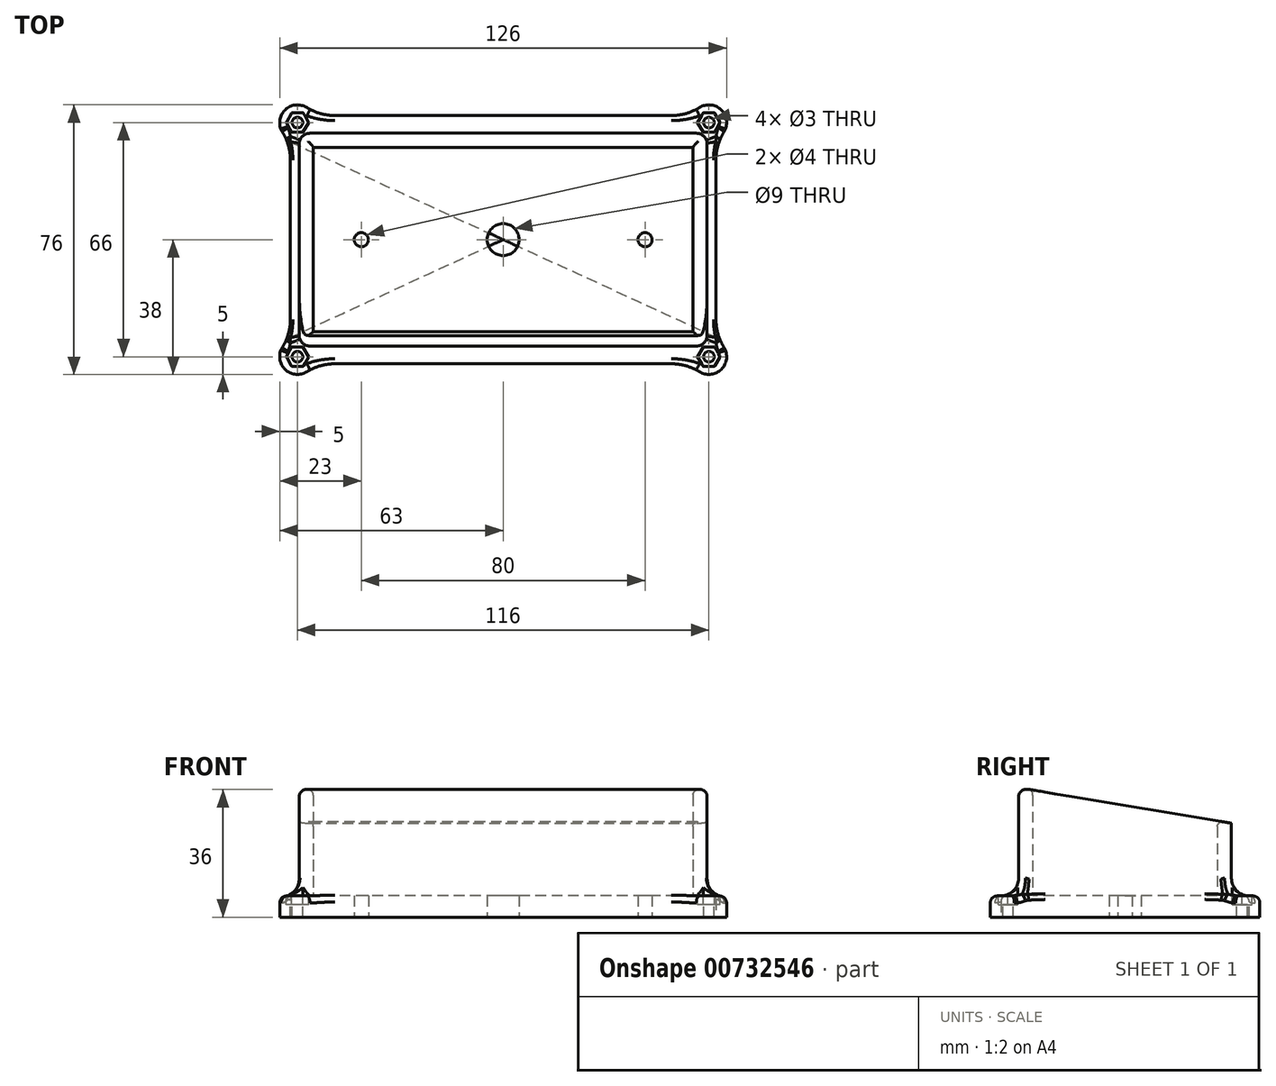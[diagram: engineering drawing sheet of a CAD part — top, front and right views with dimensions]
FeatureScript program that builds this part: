
annotation { "Feature Type Name" : "Feature", "Feature Type Description" : "" }
export const myFeature = defineFeature(function(context is Context, id is Id, definition is map)
    precondition{}
    {
        {
            var Q0;
            Q0=qCreatedBy(makeId("Top.planeOp"),FACE);
            var sketch = newSketch(context, id + "F0", { "sketchPlane" : qUnion([Q0])});
            skLineSegment(sketch, "E0.bottom", {"start": v(53.42, 35) * mm, "end": v(-53.42, 35) * mm});
            skLineSegment(sketch, "E0.top", {"start": v(53.42, -35) * mm, "end": v(-53.42, -35) * mm});
            skLineSegment(sketch, "E0.left", {"start": v(60, 28.42) * mm, "end": v(60, -28.42) * mm});
            skLineSegment(sketch, "E0.right", {"start": v(-60, 28.42) * mm, "end": v(-60, -28.42) * mm});
            skPoint(sketch, "E0.middle", {"position": v(0, 0) * mm});
            skLineSegment(sketch, "E1.bottom", {"start": v(58, -33) * mm, "end": v(-58, -33) * mm, "construction": true});
            skLineSegment(sketch, "E1.top", {"start": v(58, 33) * mm, "end": v(-58, 33) * mm, "construction": true});
            skLineSegment(sketch, "E1.left", {"start": v(58, 33) * mm, "end": v(58, -33) * mm, "construction": true});
            skLineSegment(sketch, "E1.right", {"start": v(-58, 33) * mm, "end": v(-58, -33) * mm, "construction": true});
            skArc(sketch, "E2", {"start": v(-53.42, 35) * mm, "mid": v(-61.54, 36.54) * mm, "end": v(-60, 28.42) * mm});
            skArc(sketch, "E3", {"start": v(-60, -28.42) * mm, "mid": v(-61.54, -36.54) * mm, "end": v(-53.42, -35) * mm});
            skArc(sketch, "E4", {"start": v(60, 28.42) * mm, "mid": v(61.54, 36.54) * mm, "end": v(53.42, 35) * mm});
            skArc(sketch, "E5", {"start": v(53.42, -35) * mm, "mid": v(61.54, -36.54) * mm, "end": v(60, -28.42) * mm});
            skPoint(sketch, "E6.orphan", {"position": v(-60, 35) * mm});
            skPoint(sketch, "E7.orphan", {"position": v(60, 35) * mm});
            skPoint(sketch, "E8.orphan", {"position": v(60, -35) * mm});
            skPoint(sketch, "E9.orphan", {"position": v(-60, -35) * mm});
            skSolve(sketch);
        }
        {
            var Q0;
            Q0 = qSketchRegion(id + "F0", true);
            extrude(context, id + "F1", {"entities" : qUnion([Q0]), "depth" : 6 * mm, "offsetDistance" : 25 * mm});
        }
        {
            var Q0;
            Q0=makeQuery(id+"F1.opExtrude","SWEPT_EDGE",EDGE,{"disambiguationData":[OSD([sQuery(id+"F0.wireOp",EDGE,"E0.bottom"),sQuery(id+"F0.wireOp",EDGE,"E2")])]});
            var Q1;
            Q1=makeQuery(id+"F1.opExtrude","SWEPT_EDGE",EDGE,{"disambiguationData":[OSD([sQuery(id+"F0.wireOp",EDGE,"E0.bottom"),sQuery(id+"F0.wireOp",EDGE,"E4")])]});
            var Q2;
            Q2=makeQuery(id+"F1.opExtrude","SWEPT_EDGE",EDGE,{"disambiguationData":[OSD([sQuery(id+"F0.wireOp",EDGE,"E0.left"),sQuery(id+"F0.wireOp",EDGE,"E5")])]});
            var Q3;
            Q3=makeQuery(id+"F1.opExtrude","SWEPT_EDGE",EDGE,{"disambiguationData":[OSD([sQuery(id+"F0.wireOp",EDGE,"E0.left"),sQuery(id+"F0.wireOp",EDGE,"E4")])]});
            var Q4;
            Q4=makeQuery(id+"F1.opExtrude","SWEPT_EDGE",EDGE,{"disambiguationData":[OSD([sQuery(id+"F0.wireOp",EDGE,"E0.top"),sQuery(id+"F0.wireOp",EDGE,"E5")])]});
            var Q5;
            Q5=makeQuery(id+"F1.opExtrude","SWEPT_EDGE",EDGE,{"disambiguationData":[OSD([sQuery(id+"F0.wireOp",EDGE,"E0.top"),sQuery(id+"F0.wireOp",EDGE,"E3")])]});
            var Q6;
            Q6=makeQuery(id+"F1.opExtrude","SWEPT_EDGE",EDGE,{"disambiguationData":[OSD([sQuery(id+"F0.wireOp",EDGE,"E0.right"),sQuery(id+"F0.wireOp",EDGE,"E3")])]});
            var Q7;
            Q7=makeQuery(id+"F1.opExtrude","SWEPT_EDGE",EDGE,{"disambiguationData":[OSD([sQuery(id+"F0.wireOp",EDGE,"E0.right"),sQuery(id+"F0.wireOp",EDGE,"E2")])]});
            fillet(context, id + "F2", {"entities" : qUnion([Q0, Q1, Q2, Q3, Q4, Q5, Q6, Q7]), "radius" : 15 * mm, "tangentPropagation" : true, "allowEdgeOverflow" : false});
        }
        {
            var Q0;
            Q0=makeQuery(id+"F1.opExtrude","CAP_FACE",FACE,{"disambiguationData":[OSD([sQuery(id+"F0.wireOp",EDGE,"E0.bottom"),sQuery(id+"F0.wireOp",EDGE,"E0.top"),sQuery(id+"F0.wireOp",EDGE,"E0.left"),sQuery(id+"F0.wireOp",EDGE,"E0.right"),sQuery(id+"F0.wireOp",EDGE,"E2"),sQuery(id+"F0.wireOp",EDGE,"E3"),sQuery(id+"F0.wireOp",EDGE,"E4"),sQuery(id+"F0.wireOp",EDGE,"E5")])],"isStart":false});
            var sketch = newSketch(context, id + "F3", { "sketchPlane" : qUnion([Q0])});
            skLineSegment(sketch, "E10.bottom", {"start": v(57.5, 30) * mm, "end": v(-57.5, 30) * mm});
            skLineSegment(sketch, "E10.top", {"start": v(57.5, -30) * mm, "end": v(-57.5, -30) * mm});
            skLineSegment(sketch, "E10.left", {"start": v(57.5, 30) * mm, "end": v(57.5, -30) * mm});
            skLineSegment(sketch, "E10.right", {"start": v(-57.5, 30) * mm, "end": v(-57.5, -30) * mm});
            skPoint(sketch, "E10.middle", {"position": v(0, 0) * mm});
            skLineSegment(sketch, "E11.bottom", {"start": v(53.5, 26) * mm, "end": v(-53.5, 26) * mm});
            skLineSegment(sketch, "E11.top", {"start": v(53.5, -26) * mm, "end": v(-53.5, -26) * mm});
            skLineSegment(sketch, "E11.left", {"start": v(53.5, 26) * mm, "end": v(53.5, -26) * mm});
            skLineSegment(sketch, "E11.right", {"start": v(-53.5, 26) * mm, "end": v(-53.5, -26) * mm});
            skSolve(sketch);
        }
        {
            var Q0;
            Q0 = qSketchRegion(id + "F3", true);
            extrude(context, id + "F4", {"entities" : qUnion([Q0]), "operationType" : NewBodyOperationType.ADD, "depth" : 30 * mm, "offsetDistance" : 25 * mm});
        }
        {
            var Q0;
            Q0=makeQuery(id+"F4.opExtrude","SWEPT_EDGE",EDGE,{"disambiguationData":[OSD([sQuery(id+"F3.wireOp",EDGE,"E10.top"),sQuery(id+"F3.wireOp",EDGE,"E10.right")])]});
            var Q1;
            Q1=makeQuery(id+"F4.opExtrude","SWEPT_EDGE",EDGE,{"disambiguationData":[OSD([sQuery(id+"F3.wireOp",EDGE,"E10.top"),sQuery(id+"F3.wireOp",EDGE,"E10.left")])]});
            var Q2;
            Q2=makeQuery(id+"F4.opExtrude","SWEPT_EDGE",EDGE,{"disambiguationData":[OSD([sQuery(id+"F3.wireOp",EDGE,"E10.bottom"),sQuery(id+"F3.wireOp",EDGE,"E10.left")])]});
            var Q3;
            Q3=makeQuery(id+"F4.opExtrude","SWEPT_EDGE",EDGE,{"disambiguationData":[OSD([sQuery(id+"F3.wireOp",EDGE,"E10.bottom"),sQuery(id+"F3.wireOp",EDGE,"E10.right")])]});
            fillet(context, id + "F5", {"entities" : qUnion([Q0, Q1, Q2, Q3]), "radius" : 3 * mm, "allowEdgeOverflow" : false});
        }
        {
            var Q0;
            Q0=makeQuery(id+"F4.opExtrude","CAP_EDGE",EDGE,{"disambiguationData":[OSD([sQuery(id+"F3.wireOp",EDGE,"E10.bottom")])],"isStart":true});
            fillet(context, id + "F6", {"entities" : qUnion([Q0]), "radius" : 5 * mm, "tangentPropagation" : true, "allowEdgeOverflow" : false});
        }
        {
            var Q0;
            Q0=makeQuery(id+"F6.opFillet","BLEND_EDGE",EDGE,{"blendedFrom":[makeQuery(id+"F4.opExtrude","CAP_EDGE",EDGE,{"disambiguationData":[OSD([sQuery(id+"F3.wireOp",EDGE,"E10.bottom")])],"isStart":true}),makeQuery(id+"F1.opExtrude","SWEPT_FACE",FACE,{"disambiguationData":[OSD([sQuery(id+"F0.wireOp",EDGE,"E0.bottom")])]})],"blendedInto":[makeQuery(id+"F1.opExtrude","SWEPT_FACE",FACE,{"disambiguationData":[OSD([sQuery(id+"F0.wireOp",EDGE,"E0.bottom")])]})]});
            fillet(context, id + "F7", {"entities" : qUnion([Q0]), "radius" : 2 * mm, "tangentPropagation" : true, "allowEdgeOverflow" : false});
        }
        {
            var Q0;
            Q0=makeQuery(id+"F4.opExtrude","SWEPT_FACE",FACE,{"disambiguationData":[OSD([sQuery(id+"F3.wireOp",EDGE,"E10.left")])]});
            var sketch = newSketch(context, id + "F8", { "sketchPlane" : qUnion([Q0])});
            skLineSegment(sketch, "E12.bottom", {"start": v(-27, 36) * mm, "end": v(30.22, 36) * mm});
            skLineSegment(sketch, "E12.right", {"start": v(30.22, 36) * mm, "end": v(30.22, 26.46) * mm});
            skPoint(sketch, "E12.middle", {"position": v(0, 24.05) * mm});
            skLineSegment(sketch, "E13", {"start": v(-27, 36) * mm, "end": v(30.22, 26.46) * mm});
            skPoint(sketch, "E12.left.start.orphan", {"position": v(-30.22, 36) * mm});
            skPoint(sketch, "E12.top.start.orphan", {"position": v(-30.22, 12.1) * mm});
            skPoint(sketch, "E14.orphan", {"position": v(30.22, 12.1) * mm});
            skSolve(sketch);
        }
        {
            var Q0;
            Q0 = qSketchRegion(id + "F8", true);
            extrude(context, id + "F9", {"entities" : qUnion([Q0]), "operationType" : NewBodyOperationType.REMOVE, "endBound" : BoundingType.THROUGH_ALL, "oppositeDirection" : true, "depth" : 25 * mm, "offsetDistance" : 25 * mm});
        }
        {
            var Q0;
            Q0=makeQuery(id+"F9.boolean.opBoolean","COPY",EDGE,{"derivedFrom":makeQuery(id+"F9.opExtrude","CAP_EDGE",EDGE,{"disambiguationData":[OSD([sQuery(id+"F8.wireOp",EDGE,"E13")])],"isStart":true})});
            var Q1;
            Q1=makeQuery(id+"F4.opExtrude","CAP_EDGE",EDGE,{"disambiguationData":[OSD([sQuery(id+"F3.wireOp",EDGE,"E10.top")])],"isStart":false});
            fillet(context, id + "F10", {"entities" : qUnion([Q0, Q1]), "radius" : 2 * mm, "tangentPropagation" : true, "allowEdgeOverflow" : false});
        }
        {
            var Q0;
            Q0=makeQuery(id+"F9.boolean.opBoolean","INTERSECT",EDGE,{"derivedFrom":[makeQuery(id+"F4.opExtrude","SWEPT_FACE",FACE,{"disambiguationData":[OSD([sQuery(id+"F3.wireOp",EDGE,"E11.left")])]}),makeQuery(id+"F9.opExtrude","SWEPT_FACE",FACE,{"disambiguationData":[OSD([sQuery(id+"F8.wireOp",EDGE,"E13")])]})]});
            var Q1;
            Q1=makeQuery(id+"F9.boolean.opBoolean","INTERSECT",EDGE,{"derivedFrom":[makeQuery(id+"F4.opExtrude","SWEPT_FACE",FACE,{"disambiguationData":[OSD([sQuery(id+"F3.wireOp",EDGE,"E11.top")])]}),makeQuery(id+"F9.opExtrude","SWEPT_FACE",FACE,{"disambiguationData":[OSD([sQuery(id+"F8.wireOp",EDGE,"E13")])]})]});
            var Q2;
            Q2=makeQuery(id+"F9.boolean.opBoolean","INTERSECT",EDGE,{"derivedFrom":[makeQuery(id+"F4.opExtrude","SWEPT_FACE",FACE,{"disambiguationData":[OSD([sQuery(id+"F3.wireOp",EDGE,"E11.right")])]}),makeQuery(id+"F9.opExtrude","SWEPT_FACE",FACE,{"disambiguationData":[OSD([sQuery(id+"F8.wireOp",EDGE,"E13")])]})]});
            var Q3;
            Q3=makeQuery(id+"F9.boolean.opBoolean","INTERSECT",EDGE,{"derivedFrom":[makeQuery(id+"F4.opExtrude","SWEPT_FACE",FACE,{"disambiguationData":[OSD([sQuery(id+"F3.wireOp",EDGE,"E11.bottom")])]}),makeQuery(id+"F9.opExtrude","SWEPT_FACE",FACE,{"disambiguationData":[OSD([sQuery(id+"F8.wireOp",EDGE,"E13")])]})]});
            fillet(context, id + "F11", {"entities" : qUnion([Q0, Q1, Q2, Q3]), "radius" : 1.5 * mm, "tangentPropagation" : true, "allowEdgeOverflow" : false});
        }
        {
            var Q0;
            Q0=makeQuery(id+"F4.boolean.opBoolean","SPLIT",FACE,{"disambiguationData":[TD([makeQuery(id+"F4.opExtrude","SWEPT_FACE",FACE,{"disambiguationData":[OSD([sQuery(id+"F3.wireOp",EDGE,"E11.bottom")])]})])],"derivedFrom":makeQuery(id+"F1.opExtrude","CAP_FACE",FACE,{"disambiguationData":[OSD([sQuery(id+"F0.wireOp",EDGE,"E0.bottom"),sQuery(id+"F0.wireOp",EDGE,"E0.top"),sQuery(id+"F0.wireOp",EDGE,"E0.left"),sQuery(id+"F0.wireOp",EDGE,"E0.right"),sQuery(id+"F0.wireOp",EDGE,"E2"),sQuery(id+"F0.wireOp",EDGE,"E3"),sQuery(id+"F0.wireOp",EDGE,"E4"),sQuery(id+"F0.wireOp",EDGE,"E5")])],"isStart":false})});
            var sketch = newSketch(context, id + "F12", { "sketchPlane" : qUnion([Q0])});
            skLineSegment(sketch, "E15.bottom", {"start": v(58, 33) * mm, "end": v(-58, 33) * mm, "construction": true});
            skLineSegment(sketch, "E15.top", {"start": v(58, -33) * mm, "end": v(-58, -33) * mm, "construction": true});
            skLineSegment(sketch, "E15.left", {"start": v(58, 33) * mm, "end": v(58, -33) * mm, "construction": true});
            skLineSegment(sketch, "E15.right", {"start": v(-58, 33) * mm, "end": v(-58, -33) * mm, "construction": true});
            skPoint(sketch, "E15.middle", {"position": v(0, 0) * mm});
            skCircle(sketch, "E16.cCircle", {"center": v(-58, 33) * mm, "radius": 2.75 * mm, "construction": true});
            skLineSegment(sketch, "E16.0", {"start": v(-56.41, 30.25) * mm, "end": v(-59.59, 30.25) * mm});
            skLineSegment(sketch, "E16.1", {"start": v(-59.59, 30.25) * mm, "end": v(-61.18, 33) * mm});
            skLineSegment(sketch, "E16.2", {"start": v(-61.18, 33) * mm, "end": v(-59.59, 35.75) * mm});
            skLineSegment(sketch, "E16.3", {"start": v(-59.59, 35.75) * mm, "end": v(-56.41, 35.75) * mm});
            skLineSegment(sketch, "E16.4", {"start": v(-56.41, 35.75) * mm, "end": v(-54.82, 33) * mm});
            skLineSegment(sketch, "E16.5", {"start": v(-54.82, 33) * mm, "end": v(-56.41, 30.25) * mm});
            skPoint(sketch, "E16.0.midPoint", {"position": v(-58, 30.25) * mm});
            skCircle(sketch, "E17.cCircle", {"center": v(58, 33) * mm, "radius": 2.75 * mm, "construction": true});
            skLineSegment(sketch, "E17.0", {"start": v(54.82, 33) * mm, "end": v(56.41, 35.75) * mm});
            skLineSegment(sketch, "E17.1", {"start": v(56.41, 35.75) * mm, "end": v(59.59, 35.75) * mm});
            skLineSegment(sketch, "E17.2", {"start": v(59.59, 35.75) * mm, "end": v(61.18, 33) * mm});
            skLineSegment(sketch, "E17.3", {"start": v(61.18, 33) * mm, "end": v(59.59, 30.25) * mm});
            skLineSegment(sketch, "E17.4", {"start": v(59.59, 30.25) * mm, "end": v(56.41, 30.25) * mm});
            skLineSegment(sketch, "E17.5", {"start": v(56.41, 30.25) * mm, "end": v(54.82, 33) * mm});
            skPoint(sketch, "E17.0.midPoint", {"position": v(55.62, 34.38) * mm});
            skCircle(sketch, "E18.cCircle", {"center": v(58, -33) * mm, "radius": 2.75 * mm, "construction": true});
            skPoint(sketch, "E18.cCircle.perimeterSnap0", {"position": v(55.62, 31.62) * mm});
            skLineSegment(sketch, "E18.0", {"start": v(56.41, -35.75) * mm, "end": v(54.82, -33) * mm});
            skLineSegment(sketch, "E18.1", {"start": v(54.82, -33) * mm, "end": v(56.41, -30.25) * mm});
            skLineSegment(sketch, "E18.2", {"start": v(56.41, -30.25) * mm, "end": v(59.59, -30.25) * mm});
            skLineSegment(sketch, "E18.3", {"start": v(59.59, -30.25) * mm, "end": v(61.18, -33) * mm});
            skLineSegment(sketch, "E18.4", {"start": v(61.18, -33) * mm, "end": v(59.59, -35.75) * mm});
            skLineSegment(sketch, "E18.5", {"start": v(59.59, -35.75) * mm, "end": v(56.41, -35.75) * mm});
            skPoint(sketch, "E18.0.midPoint", {"position": v(55.62, -34.38) * mm});
            skPoint(sketch, "E18.0.midPoint.positionSnap0", {"position": v(55.62, 31.63) * mm});
            skCircle(sketch, "E19.cCircle", {"center": v(-58, -33) * mm, "radius": 2.75 * mm, "construction": true});
            skLineSegment(sketch, "E19.0", {"start": v(-59.59, -35.75) * mm, "end": v(-61.18, -33) * mm});
            skLineSegment(sketch, "E19.1", {"start": v(-61.18, -33) * mm, "end": v(-59.59, -30.25) * mm});
            skLineSegment(sketch, "E19.2", {"start": v(-59.59, -30.25) * mm, "end": v(-56.41, -30.25) * mm});
            skLineSegment(sketch, "E19.3", {"start": v(-56.41, -30.25) * mm, "end": v(-54.82, -33) * mm});
            skLineSegment(sketch, "E19.4", {"start": v(-54.82, -33) * mm, "end": v(-56.41, -35.75) * mm});
            skLineSegment(sketch, "E19.5", {"start": v(-56.41, -35.75) * mm, "end": v(-59.59, -35.75) * mm});
            skPoint(sketch, "E19.0.midPoint", {"position": v(-60.38, -34.37) * mm});
            skSolve(sketch);
        }
        {
            var Q0;
            Q0 = qSketchRegion(id + "F12", true);
            extrude(context, id + "F13", {"entities" : qUnion([Q0]), "operationType" : NewBodyOperationType.REMOVE, "oppositeDirection" : true, "depth" : 2.5 * mm, "offsetDistance" : 25 * mm, "hasSecondDirection" : true, "secondDirectionOppositeDirection" : false, "secondDirectionDepth" : 15 * mm});
        }
        {
            var Q0;
            Q0=makeQuery(id+"F4.boolean.opBoolean","SPLIT",FACE,{"disambiguationData":[TD([makeQuery(id+"F4.opExtrude","SWEPT_FACE",FACE,{"disambiguationData":[OSD([sQuery(id+"F3.wireOp",EDGE,"E11.bottom")])]})])],"derivedFrom":makeQuery(id+"F1.opExtrude","CAP_FACE",FACE,{"disambiguationData":[OSD([sQuery(id+"F0.wireOp",EDGE,"E0.bottom"),sQuery(id+"F0.wireOp",EDGE,"E0.top"),sQuery(id+"F0.wireOp",EDGE,"E0.left"),sQuery(id+"F0.wireOp",EDGE,"E0.right"),sQuery(id+"F0.wireOp",EDGE,"E2"),sQuery(id+"F0.wireOp",EDGE,"E3"),sQuery(id+"F0.wireOp",EDGE,"E4"),sQuery(id+"F0.wireOp",EDGE,"E5")])],"isStart":false})});
            var sketch = newSketch(context, id + "F14", { "sketchPlane" : qUnion([Q0])});
            skLineSegment(sketch, "E20.bottom", {"start": v(-58, 33) * mm, "end": v(58, 33) * mm, "construction": true});
            skLineSegment(sketch, "E20.top", {"start": v(-58, -33) * mm, "end": v(58, -33) * mm, "construction": true});
            skLineSegment(sketch, "E20.left", {"start": v(-58, 33) * mm, "end": v(-58, -33) * mm, "construction": true});
            skLineSegment(sketch, "E20.right", {"start": v(58, 33) * mm, "end": v(58, -33) * mm, "construction": true});
            skPoint(sketch, "E20.middle", {"position": v(0, 0) * mm});
            skCircle(sketch, "E21", {"center": v(-58, 33) * mm, "radius": 1.5 * mm});
            skCircle(sketch, "E22", {"center": v(-58, -33) * mm, "radius": 1.5 * mm});
            skCircle(sketch, "E23", {"center": v(58, 33) * mm, "radius": 1.5 * mm});
            skCircle(sketch, "E24", {"center": v(58, -33) * mm, "radius": 1.5 * mm});
            skSolve(sketch);
        }
        {
            var Q0;
            Q0 = qSketchRegion(id + "F14", true);
            extrude(context, id + "F15", {"entities" : qUnion([Q0]), "operationType" : NewBodyOperationType.REMOVE, "oppositeDirection" : true, "depth" : 25 * mm, "offsetDistance" : 25 * mm});
        }
        {
            var Q0;
            Q0=makeQuery(id+"F1.opExtrude","CAP_FACE",FACE,{"disambiguationData":[OSD([sQuery(id+"F0.wireOp",EDGE,"E0.bottom"),sQuery(id+"F0.wireOp",EDGE,"E0.top"),sQuery(id+"F0.wireOp",EDGE,"E0.left"),sQuery(id+"F0.wireOp",EDGE,"E0.right"),sQuery(id+"F0.wireOp",EDGE,"E2"),sQuery(id+"F0.wireOp",EDGE,"E3"),sQuery(id+"F0.wireOp",EDGE,"E4"),sQuery(id+"F0.wireOp",EDGE,"E5")])],"isStart":true});
            var sketch = newSketch(context, id + "F16", { "sketchPlane" : qUnion([Q0])});
            skLineSegment(sketch, "E25", {"start": v(-72.3, 0) * mm, "end": v(71.2, 0) * mm, "construction": true});
            skCircle(sketch, "E26", {"center": v(0, 0) * mm, "radius": 4.5 * mm});
            skCircle(sketch, "E27", {"center": v(40, 0) * mm, "radius": 2 * mm});
            skCircle(sketch, "E28", {"center": v(-40, 0) * mm, "radius": 2 * mm});
            skSolve(sketch);
        }
        {
            var Q0;
            Q0 = qSketchRegion(id + "F16", true);
            extrude(context, id + "F17", {"entities" : qUnion([Q0]), "operationType" : NewBodyOperationType.REMOVE, "oppositeDirection" : true, "depth" : 25 * mm, "offsetDistance" : 25 * mm});
        }
    });
